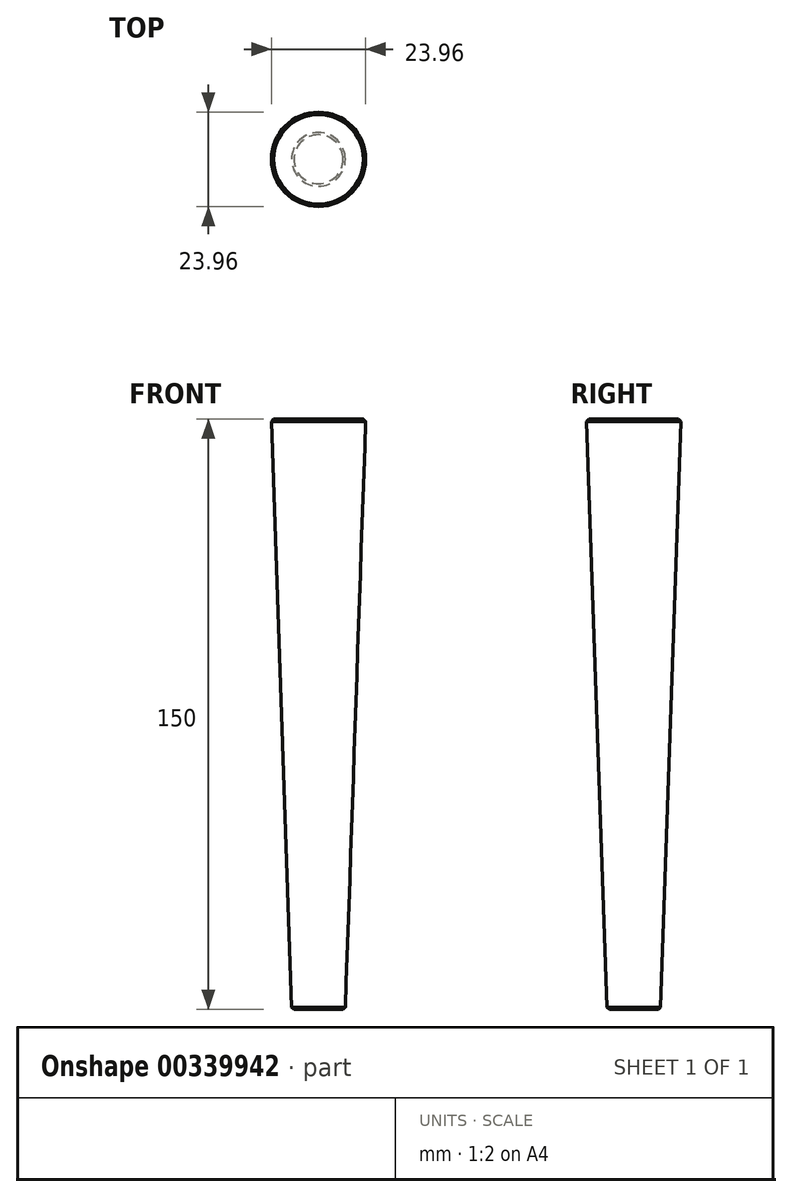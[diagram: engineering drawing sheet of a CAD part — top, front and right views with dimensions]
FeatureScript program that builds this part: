
annotation { "Feature Type Name" : "Feature", "Feature Type Description" : "" }
export const myFeature = defineFeature(function(context is Context, id is Id, definition is map)
    precondition{}
    {
        {
            var Q0;
            Q0=qCreatedBy(makeId("Top.planeOp"),FACE);
            var sketch = newSketch(context, id + "F0", { "sketchPlane" : qUnion([Q0])});
            skCircle(sketch, "E0", {"center": v(0, 0) * mm, "radius": 6.8 * mm});
            skSolve(sketch);
        }
        {
            var Q0;
            Q0=qCreatedBy(makeId("Top.planeOp"),FACE);
            cPlane(context, id + "F1", {"entities" : qUnion([Q0]), "cplaneType" : CPlaneType.OFFSET, "offset" : 150 * mm, "width" : 150 * mm, "height" : 150 * mm});
        }
        {
            var Q0;
            Q0=qCreatedBy(id+"F1.planeOp",FACE);
            var sketch = newSketch(context, id + "F2", { "sketchPlane" : qUnion([Q0])});
            skCircle(sketch, "E1", {"center": v(0, 0) * mm, "radius": 12 * mm});
            skSolve(sketch);
        }
        {
            var Q0;
            Q0=makeQuery(id+"F2.imprint","IMPRINT",FACE,{"disambiguationData":[TD([[makeQuery(id+"F2.imprint","IMPRINT",EDGE,{"derivedFrom":sQuery(id+"F2.wireOp",EDGE,"E1")}),1.0]])]});
            var Q1;
            Q1=makeQuery(id+"F0.imprint","IMPRINT",FACE,{"disambiguationData":[TD([[makeQuery(id+"F0.imprint","IMPRINT",EDGE,{"derivedFrom":sQuery(id+"F0.wireOp",EDGE,"E0")}),1.0]])]});
            loft(context, id + "F3", {"sheetProfilesArray" : [{ "sheetProfileEntities" : qUnion([Q0]) }, { "sheetProfileEntities" : qUnion([Q1]) }]});
        }
        {
            var Q0;
            Q0=makeQuery(id+"F3.opLoft","MID_CAP_EDGE",EDGE,{"disambiguationData":[OSD([sQuery(id+"F0.wireOp",EDGE,"E0"),sQuery(id+"F2.wireOp",EDGE,"E1")])],"capPos":1.0});
            var Q1;
            Q1=makeQuery(id+"F3.opLoft","MID_CAP_EDGE",EDGE,{"disambiguationData":[OSD([sQuery(id+"F2.wireOp",EDGE,"E1")])],"capPos":0.0});
            chamfer(context, id + "F4", {"entities" : qUnion([Q0, Q1]), "width" : 0.6 * mm, "tangentPropagation" : true});
        }
    });
